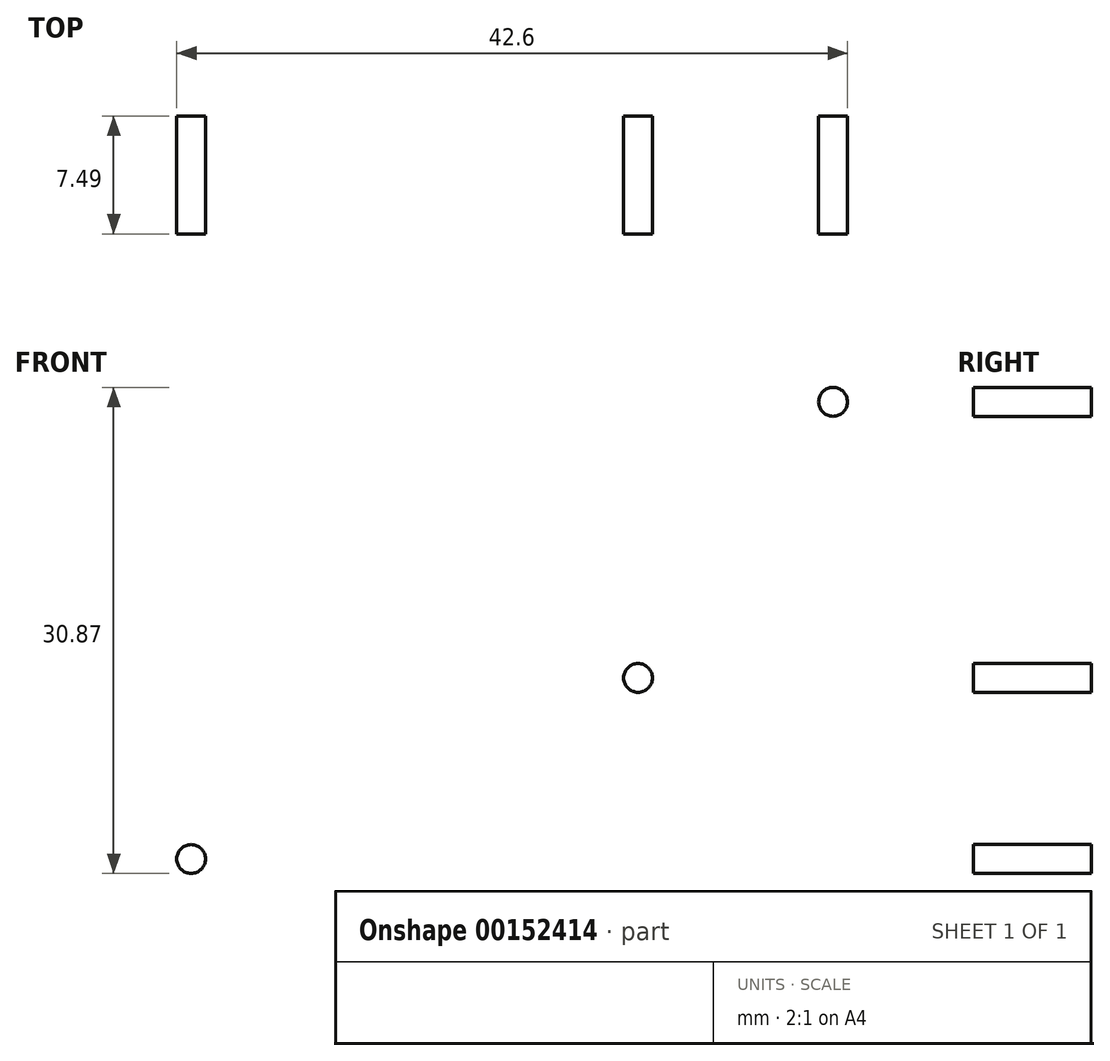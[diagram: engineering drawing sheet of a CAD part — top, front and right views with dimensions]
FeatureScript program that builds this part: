
annotation { "Feature Type Name" : "Feature", "Feature Type Description" : "" }
export const myFeature = defineFeature(function(context is Context, id is Id, definition is map)
    precondition{}
    {
        {
            var Q0;
            Q0=qCreatedBy(makeId("Front.planeOp"),FACE);
            var sketch = newSketch(context, id + "F0", { "sketchPlane" : qUnion([Q0])});
            skCircle(sketch, "E0", {"center": v(-16.37, 9.46) * mm, "radius": 0.92 * mm});
            skCircle(sketch, "E1", {"center": v(-57.14, -19.57) * mm, "radius": 0.92 * mm});
            skSolve(sketch);
        }
        {
            var Q0;
            Q0=makeQuery(id+"F0.imprint","IMPRINT",FACE,{"disambiguationData":[TD([[makeQuery(id+"F0.imprint","IMPRINT",EDGE,{"derivedFrom":sQuery(id+"F0.wireOp",EDGE,"E0")}),1.0]])]});
            extrude(context, id + "F1", {"entities" : qUnion([Q0]), "depth" : 7.5 * mm});
        }
        {
            var Q0;
            Q0=qCreatedBy(makeId("Front.planeOp"),FACE);
            var sketch = newSketch(context, id + "F2", { "sketchPlane" : qUnion([Q0])});
            skCircle(sketch, "E2", {"center": v(-28.75, -8.07) * mm, "radius": 0.92 * mm});
            skSolve(sketch);
        }
        {
            var Q0;
            Q0=makeQuery(id+"F2.imprint","IMPRINT",FACE,{"disambiguationData":[TD([[makeQuery(id+"F2.imprint","IMPRINT",EDGE,{"derivedFrom":sQuery(id+"F2.wireOp",EDGE,"E2")}),1.0]])]});
            extrude(context, id + "F3", {"entities" : qUnion([Q0]), "depth" : 7.5 * mm});
        }
        {
            var Q0;
            Q0=makeQuery(id+"F0.imprint","IMPRINT",FACE,{"disambiguationData":[TD([[makeQuery(id+"F0.imprint","IMPRINT",EDGE,{"derivedFrom":sQuery(id+"F0.wireOp",EDGE,"E1")}),1.0]])]});
            extrude(context, id + "F4", {"entities" : qUnion([Q0]), "depth" : 7.5 * mm});
        }
    });
